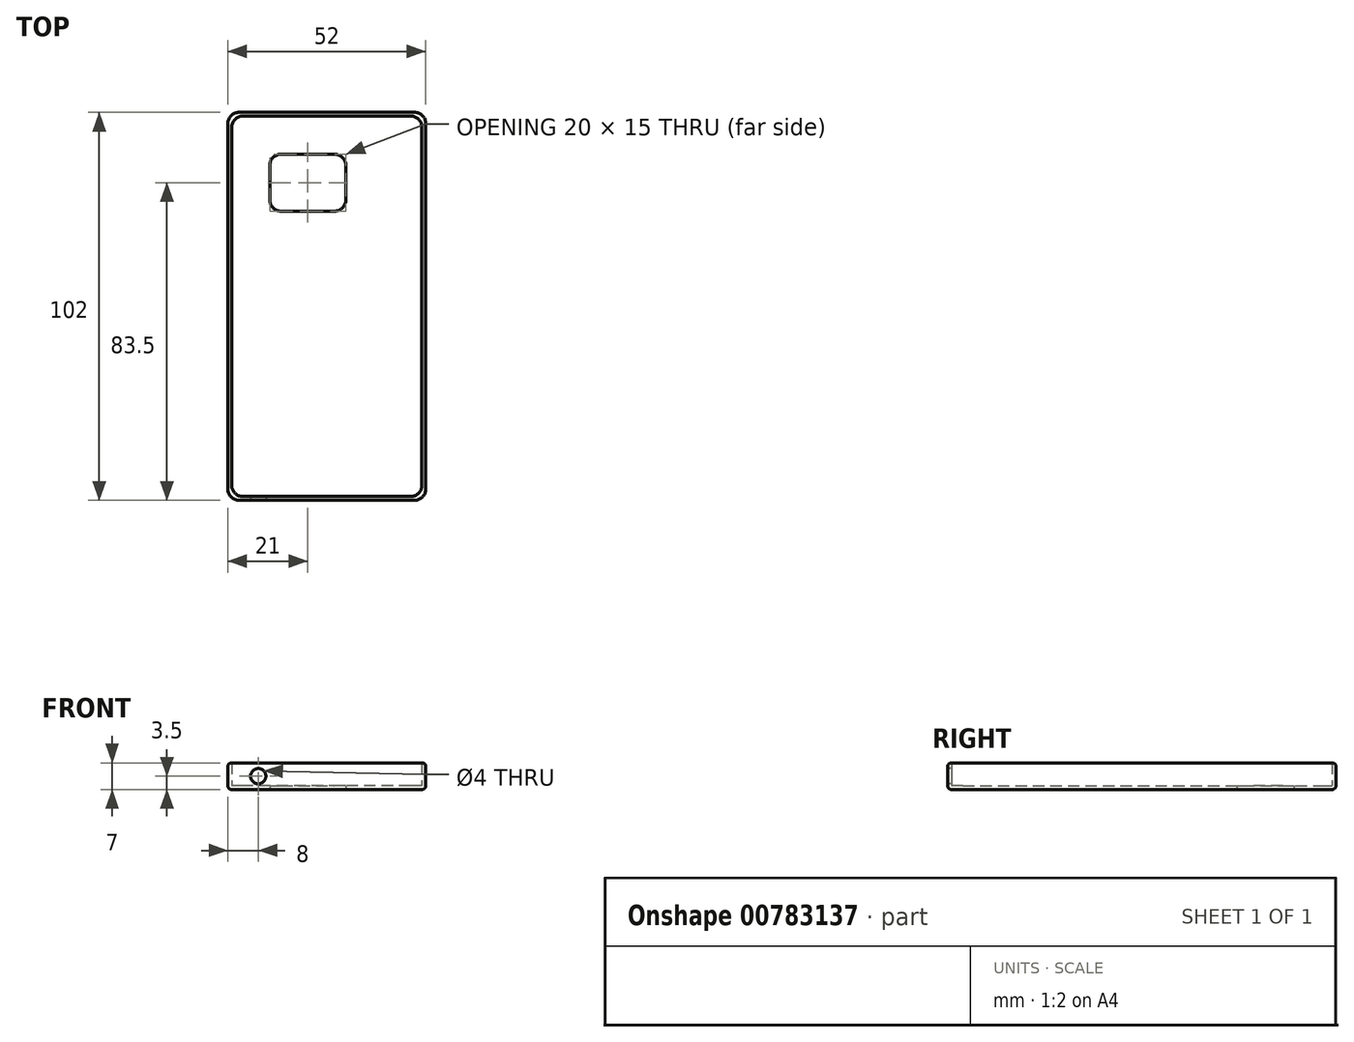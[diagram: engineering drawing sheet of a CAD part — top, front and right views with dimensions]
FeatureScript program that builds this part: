
annotation { "Feature Type Name" : "Feature", "Feature Type Description" : "" }
export const myFeature = defineFeature(function(context is Context, id is Id, definition is map)
    precondition{}
    {
        {
            var Q0;
            Q0=qCreatedBy(makeId("Top.planeOp"),FACE);
            var sketch = newSketch(context, id + "F0", { "sketchPlane" : qUnion([Q0])});
            skLineSegment(sketch, "E0.bottom", {"start": v(-22, 50) * mm, "end": v(22, 50) * mm});
            skLineSegment(sketch, "E0.top", {"start": v(-22, -50) * mm, "end": v(22, -50) * mm});
            skLineSegment(sketch, "E0.left", {"start": v(-25, 47) * mm, "end": v(-25, -47) * mm});
            skLineSegment(sketch, "E0.right", {"start": v(25, 47) * mm, "end": v(25, -47) * mm});
            skPoint(sketch, "E0.middle", {"position": v(0, 0) * mm});
            skLineSegment(sketch, "E1.bottom", {"start": v(-12, 40) * mm, "end": v(2, 40) * mm});
            skLineSegment(sketch, "E1.top", {"start": v(-12, 25) * mm, "end": v(2, 25) * mm});
            skLineSegment(sketch, "E1.left", {"start": v(-15, 37) * mm, "end": v(-15, 28) * mm});
            skLineSegment(sketch, "E1.right", {"start": v(5, 37) * mm, "end": v(5, 28) * mm});
            skLineSegment(sketch, "E2.0", {"start": v(26, 48) * mm, "end": v(26, -48) * mm});
            skLineSegment(sketch, "E2.1", {"start": v(-23, 51) * mm, "end": v(23, 51) * mm});
            skLineSegment(sketch, "E2.2", {"start": v(-26, 48) * mm, "end": v(-26, -48) * mm});
            skLineSegment(sketch, "E2.3", {"start": v(-23, -51) * mm, "end": v(23, -51) * mm});
            skPoint(sketch, "E3.visualSharp", {"position": v(-15, 40) * mm});
            skArc(sketch, "E3.filletArc", {"start": v(-12, 40) * mm, "mid": v(-14.12, 39.12) * mm, "end": v(-15, 37) * mm});
            skPoint(sketch, "E4.visualSharp", {"position": v(5, 40) * mm});
            skArc(sketch, "E4.filletArc", {"start": v(5, 37) * mm, "mid": v(4.12, 39.12) * mm, "end": v(2, 40) * mm});
            skPoint(sketch, "E5.visualSharp", {"position": v(5, 25) * mm});
            skArc(sketch, "E5.filletArc", {"start": v(2, 25) * mm, "mid": v(4.12, 25.88) * mm, "end": v(5, 28) * mm});
            skPoint(sketch, "E6.visualSharp", {"position": v(-15, 25) * mm});
            skArc(sketch, "E6.filletArc", {"start": v(-15, 28) * mm, "mid": v(-14.12, 25.88) * mm, "end": v(-12, 25) * mm});
            skPoint(sketch, "E7.visualSharp", {"position": v(25, 50) * mm});
            skArc(sketch, "E7.filletArc", {"start": v(25, 47) * mm, "mid": v(24.12, 49.12) * mm, "end": v(22, 50) * mm});
            skPoint(sketch, "E8.visualSharp", {"position": v(-25, 50) * mm});
            skArc(sketch, "E8.filletArc", {"start": v(-22, 50) * mm, "mid": v(-24.12, 49.12) * mm, "end": v(-25, 47) * mm});
            skPoint(sketch, "E9.visualSharp", {"position": v(26, 51) * mm});
            skArc(sketch, "E9.filletArc", {"start": v(26, 48) * mm, "mid": v(25.12, 50.12) * mm, "end": v(23, 51) * mm});
            skPoint(sketch, "E10.visualSharp", {"position": v(-26, 51) * mm});
            skArc(sketch, "E10.filletArc", {"start": v(-23, 51) * mm, "mid": v(-25.12, 50.12) * mm, "end": v(-26, 48) * mm});
            skPoint(sketch, "E11.visualSharp", {"position": v(25, -50) * mm});
            skArc(sketch, "E11.filletArc", {"start": v(22, -50) * mm, "mid": v(24.12, -49.12) * mm, "end": v(25, -47) * mm});
            skPoint(sketch, "E12.visualSharp", {"position": v(26, -51) * mm});
            skArc(sketch, "E12.filletArc", {"start": v(23, -51) * mm, "mid": v(25.12, -50.12) * mm, "end": v(26, -48) * mm});
            skPoint(sketch, "E13.visualSharp", {"position": v(-25, -50) * mm});
            skArc(sketch, "E13.filletArc", {"start": v(-25, -47) * mm, "mid": v(-24.12, -49.12) * mm, "end": v(-22, -50) * mm});
            skPoint(sketch, "E14.visualSharp", {"position": v(-26, -51) * mm});
            skArc(sketch, "E14.filletArc", {"start": v(-26, -48) * mm, "mid": v(-25.12, -50.12) * mm, "end": v(-23, -51) * mm});
            skSolve(sketch);
        }
        {
            var Q0;
            Q0 = qSketchRegion(id + "F0", true);
            var Q1;
            Q1=makeQuery(id+"F0.imprint","IMPRINT",FACE,{"disambiguationData":[TD([[makeQuery(id+"F0.imprint","IMPRINT",EDGE,{"derivedFrom":sQuery(id+"F0.wireOp",EDGE,"E0.bottom")}),-1.0]])]});
            extrude(context, id + "F1", {"entities" : qUnion([Q0, Q1]), "depth" : 1 * mm, "offsetDistance" : 25 * mm});
        }
        {
            var Q0;
            Q0 = qSketchRegion(id + "F0", true);
            extrude(context, id + "F2", {"entities" : qUnion([Q0]), "operationType" : NewBodyOperationType.ADD, "depth" : 7 * mm, "offsetDistance" : 25 * mm});
        }
        {
            var Q0;
            Q0=makeQuery(id+"F1.opExtrude","CAP_EDGE",EDGE,{"disambiguationData":[OSD([sQuery(id+"F0.wireOp",EDGE,"E2.0")])],"isStart":true});
            var Q1;
            Q1=makeQuery(id+"F2.opExtrude","CAP_EDGE",EDGE,{"disambiguationData":[OSD([sQuery(id+"F0.wireOp",EDGE,"E2.2")])],"isStart":false});
            fillet(context, id + "F3", {"entities" : qUnion([Q0, Q1]), "radius" : 1 * mm, "tangentPropagation" : true, "allowEdgeOverflow" : false});
        }
        {
            var Q0;
            {var subQ0=sQuery(id+"F0.wireOp",EDGE,"E2.3");Q0=makeQuery(id+"F2.boolean.opBoolean","MERGE",FACE,{"derivedFrom":[makeQuery(id+"F1.opExtrude","SWEPT_FACE",FACE,{"disambiguationData":[OSD([subQ0])]}),makeQuery(id+"F2.opExtrude","SWEPT_FACE",FACE,{"disambiguationData":[OSD([subQ0])]})]});}
            var sketch = newSketch(context, id + "F4", { "sketchPlane" : qUnion([Q0])});
            skLineSegment(sketch, "E15.bottom", {"start": v(-23, 6) * mm, "end": v(23, 6) * mm});
            skLineSegment(sketch, "E15.top", {"start": v(-23, 1) * mm, "end": v(23, 1) * mm});
            skLineSegment(sketch, "E15.left", {"start": v(-23, 6) * mm, "end": v(-23, 1) * mm});
            skLineSegment(sketch, "E15.right", {"start": v(23, 6) * mm, "end": v(23, 1) * mm});
            skLineSegment(sketch, "E16.bottom", {"start": v(-2.9, 6) * mm, "end": v(2.9, 6) * mm});
            skLineSegment(sketch, "E16.top", {"start": v(-2.9, 1.21) * mm, "end": v(2.9, 1.21) * mm});
            skLineSegment(sketch, "E16.left", {"start": v(-3.9, 5) * mm, "end": v(-3.9, 2.21) * mm});
            skLineSegment(sketch, "E16.right", {"start": v(3.9, 5) * mm, "end": v(3.9, 2.21) * mm});
            skPoint(sketch, "E16.middle", {"position": v(0, 3.6) * mm});
            skPoint(sketch, "E17.visualSharp", {"position": v(-3.9, 6) * mm});
            skArc(sketch, "E17.filletArc", {"start": v(-2.9, 6) * mm, "mid": v(-3.6, 5.7) * mm, "end": v(-3.9, 5) * mm});
            skPoint(sketch, "E18.visualSharp", {"position": v(3.9, 6) * mm});
            skArc(sketch, "E18.filletArc", {"start": v(3.9, 5) * mm, "mid": v(3.6, 5.7) * mm, "end": v(2.9, 6) * mm});
            skPoint(sketch, "E19.visualSharp", {"position": v(3.9, 1.21) * mm});
            skArc(sketch, "E19.filletArc", {"start": v(2.9, 1.21) * mm, "mid": v(3.6, 1.5) * mm, "end": v(3.9, 2.21) * mm});
            skPoint(sketch, "E20.visualSharp", {"position": v(-3.9, 1.21) * mm});
            skArc(sketch, "E20.filletArc", {"start": v(-3.9, 2.21) * mm, "mid": v(-3.6, 1.5) * mm, "end": v(-2.9, 1.21) * mm});
            skCircle(sketch, "E21", {"center": v(-18, 3.5) * mm, "radius": 2 * mm});
            skSolve(sketch);
        }
        {
            var Q0;
            Q0=makeQuery(id+"F4.imprint","IMPRINT",FACE,{"disambiguationData":[TD([[makeQuery(id+"F4.imprint","IMPRINT",EDGE,{"derivedFrom":sQuery(id+"F4.wireOp",EDGE,"E16.bottom")}),1.0]])]});
            var Q1;
            Q1=makeQuery(id+"F4.imprint","IMPRINT",FACE,{"disambiguationData":[TD([[makeQuery(id+"F4.imprint","IMPRINT",EDGE,{"derivedFrom":sQuery(id+"F4.wireOp",EDGE,"E21")}),1.0]])]});
            extrude(context, id + "F5", {"entities" : qUnion([Q0, Q1]), "operationType" : NewBodyOperationType.REMOVE, "endBound" : BoundingType.UP_TO_NEXT, "oppositeDirection" : true, "depth" : 25 * mm, "offsetDistance" : 25 * mm});
        }
    });
